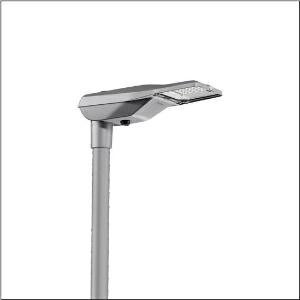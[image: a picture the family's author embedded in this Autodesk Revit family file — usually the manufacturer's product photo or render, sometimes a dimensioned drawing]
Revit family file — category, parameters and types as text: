
# Revit family: streetlight_sl_21_iq_micro___st1_0a_5xe1d31u08cb_b584
name_source: partatom
category: Lighting Fixtures
units: mm (PartAtom-declared; Revit-internal decimal feet)

## family parameters
Cut with Voids When Loaded = No
Host = Face
Light Source = No
Part Type = Normal
Room Calculation Point = No
Round Connector Dimension = Use Diameter
Shared = No

## types (1)
- --- (1 x LED, 2880 lm, 19.1 W, 3000K)
    Apparent Load = 19 VA
    CIE Flux Codes = 37 72 97 100 100
    Color Rendering = 70
    Color Temperature = 3000K
    Default Elevation = 1800 mm
    Description = Streetlight SL 21 iQ micro, mast luminaire, primary light control with lens, of PMMA, primary optical cover: cover, of toughened safety glass, transparent, light distribution: ST1.0a, light emission: direct distribution, primary light characteristic: asymmetric, installation type: post-top, side-entry, LED, High Power LED, rated luminous flux: 2.880lm, luminous efficacy: 151lm/W, light colour: 730, colour temperature: 3000K, control: presetting dimming logarithmic, Street-Remote, Auto-Match, Temp-Guard, Lumen-Switch, Night-Set, Smart-Wire, Light-Fading, Desk-Remote (wireless, voltage-free reading and setting of iQ features in the workshop via application-optimized NFC function/RFID function), optimised constant luminous flux control (CLO 2.0), mains connection: 220..240V, AC, 50/60Hz, start of lifetime: 19W, end of service life: 20W, reduction: 9W, luminaire housing, of diecast aluminium, powder-coated, Siteco® metallic grey (DB 702S), corrosivity category C5 mid according to DIN EN ISO 12944, please order mast flange separately, inclination adjustable: 0°, 5°, 10°, 15°, sealing non-destructively replaceable, multi-level sealing system, length: 528mm, width: 235mm, height: 110mm, mast flange for spigot size: 42mm (side-entry): 5XC10008XM4, 60/48mm (side-entry/post-top): 5XC10108XM2, 76/60mm (side-entry/post-top): 5XC10108XM1, Smart Interface below, protection rating (complete): IP66, insulation class (complete): insulation class II (safety insulation), certification: CE, ENEC, ENEC+, VDE, impact resistance: IK09, permissible operating ambient temperature for outdoor applications: -40..+50°C, standard-compliant lighting for roads and squares, packaging unit: 1 piece

Light Distribution: ST1.0a
    Height = 110 mm
    Lamp = 1 x LED
    Lamp Light Flux = 2880 lm
    Lamp Power = 19.1 W
    Lamp count = 1
    Length = 528 mm
    Luminous efficacy = 151 lm/W
    Manufacturer = Siteco
    ModVariant = No
    Model = 5XE1D31U08CB
    Number of Poles = 1
    OnlyDefault = Yes
    Power Factor = 1
    Product Name = Streetlight SL 21 iQ micro | ST1.0a
    Product group = mast luminaire | pylon top
    ProductGroupID = 6100
    Protection Class = Protection class II
    Protection Degree = IP 66
    RLX_Detail_Level = 1
    RLX_Emergency_Light_Flux = 0 lm
    RLX_Emergency_Type = 0
    RLX_Emergency_Type_DB = No
    RlxData = <blob elided: 99201 chars, md5=d36afa97>
    Socket = socket
    Standby Power = 0 W
    System Light Flux = 2880 lm
    System Power = 19 W
    Type Comments = factory setting: luminous flux: 100 % | dim-lin: 254 | 387 mA
    Type Image = l_1277290.jpg
    URL = http://relux.com
    VarID = @adj_045799
    Voltage = 0 V
    Weight = 0.00 kg
    Width = 235 mm

## geometry (parser evidence)
native form markers: Blend x4, Sweep x12
no freeform markers — native parametric forms only
